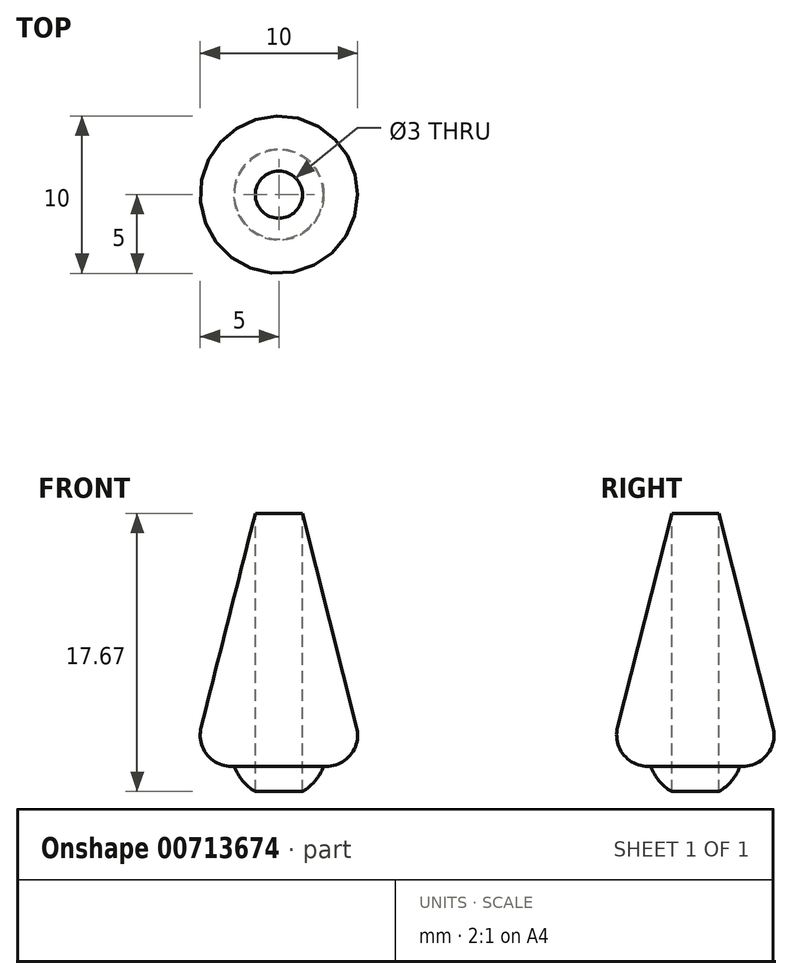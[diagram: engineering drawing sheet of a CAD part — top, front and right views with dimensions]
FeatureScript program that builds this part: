
annotation { "Feature Type Name" : "Feature", "Feature Type Description" : "" }
export const myFeature = defineFeature(function(context is Context, id is Id, definition is map)
    precondition{}
    {
        {
            var Q0;
            Q0=qCreatedBy(makeId("Front.planeOp"),FACE);
            var sketch = newSketch(context, id + "F0", { "sketchPlane" : qUnion([Q0])});
            skArc(sketch, "E0", {"start": v(-2.83, -2) * mm, "mid": v(-1.73, -3.45) * mm, "end": v(0, -4) * mm});
            skLineSegment(sketch, "E1", {"start": v(0, 0) * mm, "end": v(1105.39, 0) * mm, "construction": true});
            skArc(sketch, "E2", {"start": v(-4.94, 0.5) * mm, "mid": v(-4.54, -1.28) * mm, "end": v(-2.88, -2) * mm});
            skLineSegment(sketch, "E3", {"start": v(-3.12, -2) * mm, "end": v(-2.83, -2) * mm});
            skLineSegment(sketch, "E4", {"start": v(0, 20) * mm, "end": v(0, -4) * mm});
            skLineSegment(sketch, "E5", {"start": v(0, 20) * mm, "end": v(-4.94, 0.5) * mm});
            skPoint(sketch, "E6.trimOffspring.center.orphan", {"position": v(0, 0) * mm});
            skSolve(sketch);
        }
        {
            var Q0;
            Q0=qSketchRegion(id+"F0",true);
            var Q1;
            Q1=sQuery(id+"F0.wireOp",EDGE,"E4");
            revolve(context, id + "F1", {"surfaceOperationType" : NewSurfaceOperationType.NEW, "entities" : qUnion([Q0]), "axis" : qUnion([Q1]), "revolveType" : RevolveType.FULL});
        }
        {
            var Q0;
            Q0=qCreatedBy(makeId("Top.planeOp"),FACE);
            var sketch = newSketch(context, id + "F2", { "sketchPlane" : qUnion([Q0])});
            skCircle(sketch, "E7", {"center": v(0, 0) * mm, "radius": 1.5 * mm});
            skSolve(sketch);
        }
        {
            var Q0;
            Q0=qSketchRegion(id+"F2",true);
            extrude(context, id + "F3", {"entities" : qUnion([Q0]), "operationType" : NewBodyOperationType.REMOVE, "endBound" : BoundingType.THROUGH_ALL, "oppositeDirection" : true, "depth" : 25.4 * mm, "offsetDistance" : 25.4 * mm, "hasSecondDirection" : true, "secondDirectionBound" : SecondDirectionBoundingType.THROUGH_ALL, "secondDirectionOppositeDirection" : false, "secondDirectionDepth" : 25.4 * mm});
        }
    });
